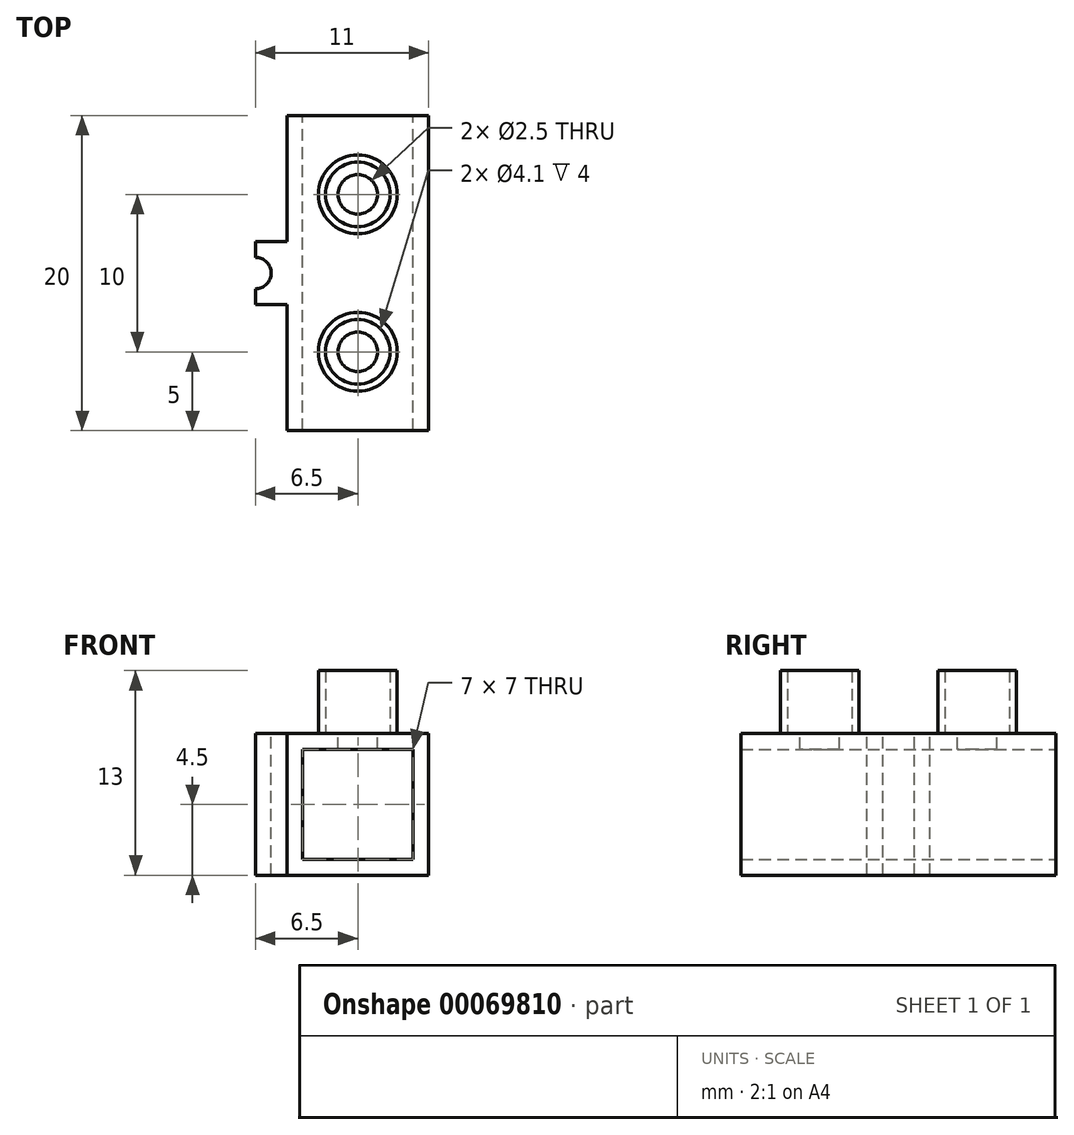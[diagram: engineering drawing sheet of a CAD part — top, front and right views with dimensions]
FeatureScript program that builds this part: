
annotation { "Feature Type Name" : "Feature", "Feature Type Description" : "" }
export const myFeature = defineFeature(function(context is Context, id is Id, definition is map)
    precondition{}
    {
        {
            var Q0;
            Q0=qCreatedBy(makeId("Front.planeOp"),FACE);
            var sketch = newSketch(context, id + "F0", { "sketchPlane" : qUnion([Q0])});
            skLineSegment(sketch, "E0.bottom", {"start": v(-3.5, 3.5) * mm, "end": v(3.5, 3.5) * mm});
            skLineSegment(sketch, "E0.top", {"start": v(-3.5, -3.5) * mm, "end": v(3.5, -3.5) * mm});
            skLineSegment(sketch, "E0.left", {"start": v(-3.5, 3.5) * mm, "end": v(-3.5, -3.5) * mm});
            skLineSegment(sketch, "E0.right", {"start": v(3.5, 3.5) * mm, "end": v(3.5, -3.5) * mm});
            skLineSegment(sketch, "E1.0", {"start": v(-4.5, -4.5) * mm, "end": v(4.5, -4.5) * mm});
            skLineSegment(sketch, "E1.1", {"start": v(-4.5, 4.5) * mm, "end": v(-4.5, -4.5) * mm});
            skLineSegment(sketch, "E1.2", {"start": v(-4.5, 4.5) * mm, "end": v(4.5, 4.5) * mm});
            skLineSegment(sketch, "E1.3", {"start": v(4.5, 4.5) * mm, "end": v(4.5, -4.5) * mm});
            skSolve(sketch);
        }
        {
            var Q0;
            Q0=makeQuery(id+"F0.imprint","IMPRINT",FACE,{"disambiguationData":[TD([[makeQuery(id+"F0.imprint","IMPRINT",EDGE,{"derivedFrom":sQuery(id+"F0.wireOp",EDGE,"E0.bottom")}),1.0]])]});
            extrude(context, id + "F1", {"entities" : qUnion([Q0]), "depth" : 10 * mm});
        }
        {
            var Q0;
            Q0=makeQuery(id+"F1.opExtrude","SWEPT_FACE",FACE,{"disambiguationData":[OSD([sQuery(id+"F0.wireOp",EDGE,"E1.2")])]});
            var sketch = newSketch(context, id + "F2", { "sketchPlane" : qUnion([Q0])});
            skLineSegment(sketch, "E2", {"start": v(-4.5, 0) * mm, "end": v(4.5, -10) * mm, "construction": true});
            skLineSegment(sketch, "E3", {"start": v(4.5, 0) * mm, "end": v(-4.5, -10) * mm, "construction": true});
            skCircle(sketch, "E4", {"center": v(0, -5) * mm, "radius": 1.25 * mm});
            skSolve(sketch);
        }
        {
            var Q0;
            Q0=makeQuery(id+"F2.imprint","IMPRINT",FACE,{"disambiguationData":[TD([[makeQuery(id+"F2.imprint","IMPRINT",EDGE,{"derivedFrom":sQuery(id+"F2.wireOp",EDGE,"E4")}),1.0]])]});
            extrude(context, id + "F3", {"entities" : qUnion([Q0]), "operationType" : NewBodyOperationType.REMOVE, "endBound" : BoundingType.UP_TO_NEXT, "oppositeDirection" : true, "depth" : 25 * mm});
        }
        {
            var Q0;
            Q0=makeQuery(id+"F1.opExtrude","SWEPT_FACE",FACE,{"disambiguationData":[OSD([sQuery(id+"F0.wireOp",EDGE,"E1.2")])]});
            var sketch = newSketch(context, id + "F4", { "sketchPlane" : qUnion([Q0])});
            skCircle(sketch, "E5", {"center": v(0, -5) * mm, "radius": 2.05 * mm});
            skCircle(sketch, "E6", {"center": v(0, -5) * mm, "radius": 2.5 * mm});
            skSolve(sketch);
        }
        {
            var Q0;
            Q0=makeQuery(id+"F4.imprint","IMPRINT",FACE,{"disambiguationData":[TD([[makeQuery(id+"F4.imprint","IMPRINT",EDGE,{"derivedFrom":sQuery(id+"F4.wireOp",EDGE,"E5")}),-1.0]])]});
            extrude(context, id + "F5", {"entities" : qUnion([Q0]), "operationType" : NewBodyOperationType.ADD, "depth" : 4 * mm});
        }
        {
            var Q0;
            {var subQ0=sQuery(id+"F0.wireOp",EDGE,"E1.1");var subQ2=sQuery(id+"F0.wireOp",EDGE,"E1.2");Q0=makeQuery(id+"F5.boolean.opBoolean","SPLIT",FACE,{"disambiguationData":[TD([makeQuery(id+"F1.opExtrude","SWEPT_FACE",FACE,{"disambiguationData":[OSD([subQ0])]})])],"derivedFrom":makeQuery(id+"F1.opExtrude","SWEPT_FACE",FACE,{"disambiguationData":[OSD([subQ2])]})});}
            var sketch = newSketch(context, id + "F6", { "sketchPlane" : qUnion([Q0])});
            skLineSegment(sketch, "E7", {"start": v(0, -5) * mm, "end": v(0, 5.18) * mm, "construction": true});
            skLineSegment(sketch, "E8", {"start": v(-4.5, 0) * mm, "end": v(-5.5, 0) * mm});
            skArc(sketch, "E9", {"start": v(-6.5, -1) * mm, "mid": v(-5.8, -0.7) * mm, "end": v(-5.5, 0) * mm});
            skLineSegment(sketch, "E10", {"start": v(-6.5, -1) * mm, "end": v(-6.5, -2) * mm});
            skLineSegment(sketch, "E11", {"start": v(-6.5, -2) * mm, "end": v(-4.5, -2) * mm});
            skArc(sketch, "E12.MirrorCS", {"start": v(6.5, -1) * mm, "mid": v(5.8, -0.7) * mm, "end": v(5.5, 0) * mm});
            skLineSegment(sketch, "E13.MirrorCS", {"start": v(6.5, -1) * mm, "end": v(6.5, -2) * mm});
            skLineSegment(sketch, "E14.MirrorCS", {"start": v(6.5, -2) * mm, "end": v(4.5, -2) * mm});
            skLineSegment(sketch, "E15.MirrorCS", {"start": v(4.5, 0) * mm, "end": v(5.5, 0) * mm});
            skSolve(sketch);
        }
        {
            var Q0;
            {var subQ1=sQuery(id+"F6.wireOp",EDGE,"E8");Q0=makeQuery(id+"F6.imprint","IMPRINT",FACE,{"disambiguationData":[TD([[makeQuery(id+"F6.imprint","IMPRINT",EDGE,{"derivedFrom":subQ1}),1.0]])]});}
            var Q1;
            Q1=makeQuery(id+"F6.imprint","IMPRINT",FACE,{"disambiguationData":[TD([[makeQuery(id+"F6.imprint","IMPRINT",EDGE,{"derivedFrom":sQuery(id+"F6.wireOp",EDGE,"E12.MirrorCS")}),1.0]])]});
            var Q2;
            Q2=makeQuery(id+"F1.opExtrude","SWEPT_FACE",FACE,{"disambiguationData":[OSD([sQuery(id+"F0.wireOp",EDGE,"E1.0")])]});
            extrude(context, id + "F7", {"entities" : qUnion([Q0, Q1]), "operationType" : NewBodyOperationType.ADD, "endBound" : BoundingType.UP_TO_SURFACE, "oppositeDirection" : true, "endBoundEntityFace" : qUnion([Q2]), "depth" : 10 * mm});
        }
        {
            var Q0;
            Q0=makeQuery(id+"F1.opExtrude","SWEPT_BODY",BODY,{"disambiguationData":[OSD([sQuery(id+"F0.wireOp",EDGE,"E0.bottom"),sQuery(id+"F0.wireOp",EDGE,"E0.top"),sQuery(id+"F0.wireOp",EDGE,"E0.left"),sQuery(id+"F0.wireOp",EDGE,"E0.right"),sQuery(id+"F0.wireOp",EDGE,"E1.0"),sQuery(id+"F0.wireOp",EDGE,"E1.1"),sQuery(id+"F0.wireOp",EDGE,"E1.2"),sQuery(id+"F0.wireOp",EDGE,"E1.3")])]});
            var Q1;
            Q1=makeQuery(id+"F7.boolean.opBoolean","MERGE",FACE,{"derivedFrom":[makeQuery(id+"F1.opExtrude","CAP_FACE",FACE,{"disambiguationData":[OSD([sQuery(id+"F0.wireOp",EDGE,"E0.bottom"),sQuery(id+"F0.wireOp",EDGE,"E0.top"),sQuery(id+"F0.wireOp",EDGE,"E0.left"),sQuery(id+"F0.wireOp",EDGE,"E0.right"),sQuery(id+"F0.wireOp",EDGE,"E1.0"),sQuery(id+"F0.wireOp",EDGE,"E1.1"),sQuery(id+"F0.wireOp",EDGE,"E1.2"),sQuery(id+"F0.wireOp",EDGE,"E1.3")])],"isStart":true}),makeQuery(id+"F7.opExtrude","SWEPT_FACE",FACE,{"disambiguationData":[OSD([sQuery(id+"F6.wireOp",EDGE,"E8")])]}),makeQuery(id+"F7.opExtrude","SWEPT_FACE",FACE,{"disambiguationData":[OSD([sQuery(id+"F6.wireOp",EDGE,"E15.MirrorCS")])]})]});
            mirror(context, id + "F8", {"operationType" : NewBodyOperationType.ADD, "entities" : qUnion([Q0]), "mirrorPlane" : qUnion([Q1])});
        }
    });
